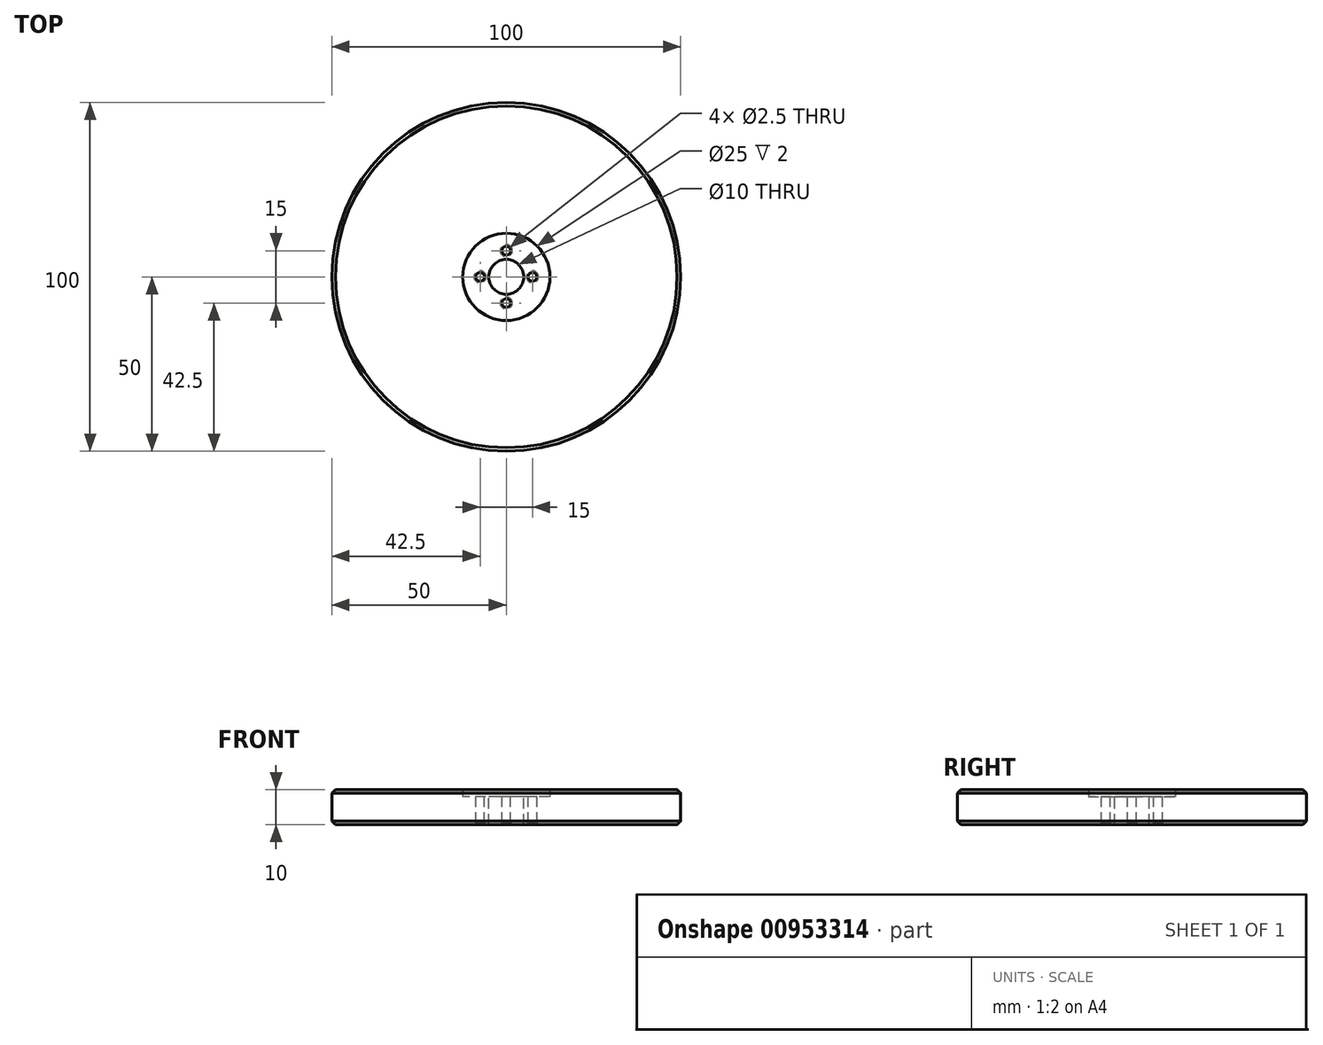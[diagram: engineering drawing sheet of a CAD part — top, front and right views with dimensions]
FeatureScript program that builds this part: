
annotation { "Feature Type Name" : "Feature", "Feature Type Description" : "" }
export const myFeature = defineFeature(function(context is Context, id is Id, definition is map)
    precondition{}
    {
        {
            var Q0;
            Q0=qCreatedBy(makeId("Top.planeOp"),FACE);
            var sketch = newSketch(context, id + "F0", { "sketchPlane" : qUnion([Q0])});
            skCircle(sketch, "E0", {"center": v(0, 0) * mm, "radius": 50 * mm});
            skCircle(sketch, "E1", {"center": v(0, 0) * mm, "radius": 12.5 * mm});
            skSolve(sketch);
        }
        {
            var Q0;
            Q0 = qSketchRegion(id + "F0", true);
            extrude(context, id + "F1", {"entities" : qUnion([Q0]), "depth" : 10 * mm, "offsetDistance" : 25 * mm});
        }
        {
            var Q0;
            Q0=makeQuery(id+"F0.imprint","IMPRINT",FACE,{"disambiguationData":[TD([[makeQuery(id+"F0.imprint","IMPRINT",EDGE,{"derivedFrom":sQuery(id+"F0.wireOp",EDGE,"E1")}),1.0]])]});
            extrude(context, id + "F2", {"entities" : qUnion([Q0]), "operationType" : NewBodyOperationType.ADD, "depth" : 8 * mm, "offsetDistance" : 25 * mm});
        }
        {
            var Q0;
            Q0=makeQuery(id+"F2.opExtrude","CAP_FACE",FACE,{"disambiguationData":[OSD([sQuery(id+"F0.wireOp",EDGE,"E1")])],"isStart":false});
            var sketch = newSketch(context, id + "F3", { "sketchPlane" : qUnion([Q0])});
            skCircle(sketch, "E2", {"center": v(0, 0) * mm, "radius": 5 * mm});
            skCircle(sketch, "E3", {"center": v(7.5, 0) * mm, "radius": 1.25 * mm});
            skCircle(sketch, "E4.1.0", {"center": v(0, 7.5) * mm, "radius": 1.25 * mm});
            skCircle(sketch, "E4.2.0", {"center": v(-7.5, 0) * mm, "radius": 1.25 * mm});
            skCircle(sketch, "E4.3.0", {"center": v(0, -7.5) * mm, "radius": 1.25 * mm});
            skSolve(sketch);
        }
        {
            var Q0;
            Q0=makeQuery(id+"F3.imprint","IMPRINT",FACE,{"disambiguationData":[TD([[makeQuery(id+"F3.imprint","IMPRINT",EDGE,{"derivedFrom":sQuery(id+"F3.wireOp",EDGE,"E2")}),1.0]])]});
            var Q1;
            Q1=makeQuery(id+"F3.imprint","IMPRINT",FACE,{"disambiguationData":[TD([[makeQuery(id+"F3.imprint","IMPRINT",EDGE,{"derivedFrom":sQuery(id+"F3.wireOp",EDGE,"E4.2.0")}),1.0]])]});
            var Q2;
            Q2=makeQuery(id+"F3.imprint","IMPRINT",FACE,{"disambiguationData":[TD([[makeQuery(id+"F3.imprint","IMPRINT",EDGE,{"derivedFrom":sQuery(id+"F3.wireOp",EDGE,"E4.1.0")}),1.0]])]});
            var Q3;
            Q3=makeQuery(id+"F3.imprint","IMPRINT",FACE,{"disambiguationData":[TD([[makeQuery(id+"F3.imprint","IMPRINT",EDGE,{"derivedFrom":sQuery(id+"F3.wireOp",EDGE,"E3")}),1.0]])]});
            var Q4;
            Q4=makeQuery(id+"F3.imprint","IMPRINT",FACE,{"disambiguationData":[TD([[makeQuery(id+"F3.imprint","IMPRINT",EDGE,{"derivedFrom":sQuery(id+"F3.wireOp",EDGE,"E4.3.0")}),1.0]])]});
            extrude(context, id + "F4", {"entities" : qUnion([Q0, Q1, Q2, Q3, Q4]), "operationType" : NewBodyOperationType.REMOVE, "oppositeDirection" : true, "depth" : 25 * mm, "offsetDistance" : 25 * mm});
        }
        {
            var Q0;
            Q0=makeQuery(id+"F1.opExtrude","CAP_EDGE",EDGE,{"disambiguationData":[OSD([sQuery(id+"F0.wireOp",EDGE,"E0")])],"isStart":true});
            var Q1;
            Q1=makeQuery(id+"F1.opExtrude","CAP_EDGE",EDGE,{"disambiguationData":[OSD([sQuery(id+"F0.wireOp",EDGE,"E0")])],"isStart":false});
            chamfer(context, id + "F5", {"entities" : qUnion([Q0, Q1]), "width" : 1 * mm, "tangentPropagation" : true});
        }
        {
            var Q0;
            {var subQ0=sQuery(id+"F0.wireOp",EDGE,"E1");Q0=makeQuery(id+"F4.boolean.opBoolean","INTERSECT",EDGE,{"derivedFrom":[makeQuery(id+"F2.boolean.opBoolean","MERGE",FACE,{"derivedFrom":[makeQuery(id+"F1.opExtrude","CAP_FACE",FACE,{"disambiguationData":[OSD([sQuery(id+"F0.wireOp",EDGE,"E0"),subQ0])],"isStart":true}),makeQuery(id+"F2.opExtrude","CAP_FACE",FACE,{"disambiguationData":[OSD([subQ0])],"isStart":true})]}),makeQuery(id+"F4.opExtrude","SWEPT_FACE",FACE,{"disambiguationData":[OSD([sQuery(id+"F3.wireOp",EDGE,"E4.2.0")])]})]});}
            var Q1;
            {var subQ0=sQuery(id+"F0.wireOp",EDGE,"E1");Q1=makeQuery(id+"F4.boolean.opBoolean","INTERSECT",EDGE,{"derivedFrom":[makeQuery(id+"F2.boolean.opBoolean","MERGE",FACE,{"derivedFrom":[makeQuery(id+"F1.opExtrude","CAP_FACE",FACE,{"disambiguationData":[OSD([sQuery(id+"F0.wireOp",EDGE,"E0"),subQ0])],"isStart":true}),makeQuery(id+"F2.opExtrude","CAP_FACE",FACE,{"disambiguationData":[OSD([subQ0])],"isStart":true})]}),makeQuery(id+"F4.opExtrude","SWEPT_FACE",FACE,{"disambiguationData":[OSD([sQuery(id+"F3.wireOp",EDGE,"E4.3.0")])]})]});}
            var Q2;
            {var subQ0=sQuery(id+"F0.wireOp",EDGE,"E1");Q2=makeQuery(id+"F4.boolean.opBoolean","INTERSECT",EDGE,{"derivedFrom":[makeQuery(id+"F2.boolean.opBoolean","MERGE",FACE,{"derivedFrom":[makeQuery(id+"F1.opExtrude","CAP_FACE",FACE,{"disambiguationData":[OSD([sQuery(id+"F0.wireOp",EDGE,"E0"),subQ0])],"isStart":true}),makeQuery(id+"F2.opExtrude","CAP_FACE",FACE,{"disambiguationData":[OSD([subQ0])],"isStart":true})]}),makeQuery(id+"F4.opExtrude","SWEPT_FACE",FACE,{"disambiguationData":[OSD([sQuery(id+"F3.wireOp",EDGE,"E3")])]})]});}
            var Q3;
            {var subQ0=sQuery(id+"F0.wireOp",EDGE,"E1");Q3=makeQuery(id+"F4.boolean.opBoolean","INTERSECT",EDGE,{"derivedFrom":[makeQuery(id+"F2.boolean.opBoolean","MERGE",FACE,{"derivedFrom":[makeQuery(id+"F1.opExtrude","CAP_FACE",FACE,{"disambiguationData":[OSD([sQuery(id+"F0.wireOp",EDGE,"E0"),subQ0])],"isStart":true}),makeQuery(id+"F2.opExtrude","CAP_FACE",FACE,{"disambiguationData":[OSD([subQ0])],"isStart":true})]}),makeQuery(id+"F4.opExtrude","SWEPT_FACE",FACE,{"disambiguationData":[OSD([sQuery(id+"F3.wireOp",EDGE,"E4.1.0")])]})]});}
            var Q4;
            Q4=makeQuery(id+"F4.boolean.opBoolean","COPY",EDGE,{"derivedFrom":makeQuery(id+"F4.opExtrude","CAP_EDGE",EDGE,{"disambiguationData":[OSD([sQuery(id+"F3.wireOp",EDGE,"E3")])],"isStart":true})});
            var Q5;
            Q5=makeQuery(id+"F4.boolean.opBoolean","COPY",EDGE,{"derivedFrom":makeQuery(id+"F4.opExtrude","CAP_EDGE",EDGE,{"disambiguationData":[OSD([sQuery(id+"F3.wireOp",EDGE,"E4.3.0")])],"isStart":true})});
            var Q6;
            Q6=makeQuery(id+"F4.boolean.opBoolean","COPY",EDGE,{"derivedFrom":makeQuery(id+"F4.opExtrude","CAP_EDGE",EDGE,{"disambiguationData":[OSD([sQuery(id+"F3.wireOp",EDGE,"E4.1.0")])],"isStart":true})});
            var Q7;
            Q7=makeQuery(id+"F4.boolean.opBoolean","COPY",EDGE,{"derivedFrom":makeQuery(id+"F4.opExtrude","CAP_EDGE",EDGE,{"disambiguationData":[OSD([sQuery(id+"F3.wireOp",EDGE,"E4.2.0")])],"isStart":true})});
            chamfer(context, id + "F6", {"entities" : qUnion([Q0, Q1, Q2, Q3, Q4, Q5, Q6, Q7]), "width" : .5 * mm, "tangentPropagation" : true});
        }
    });
